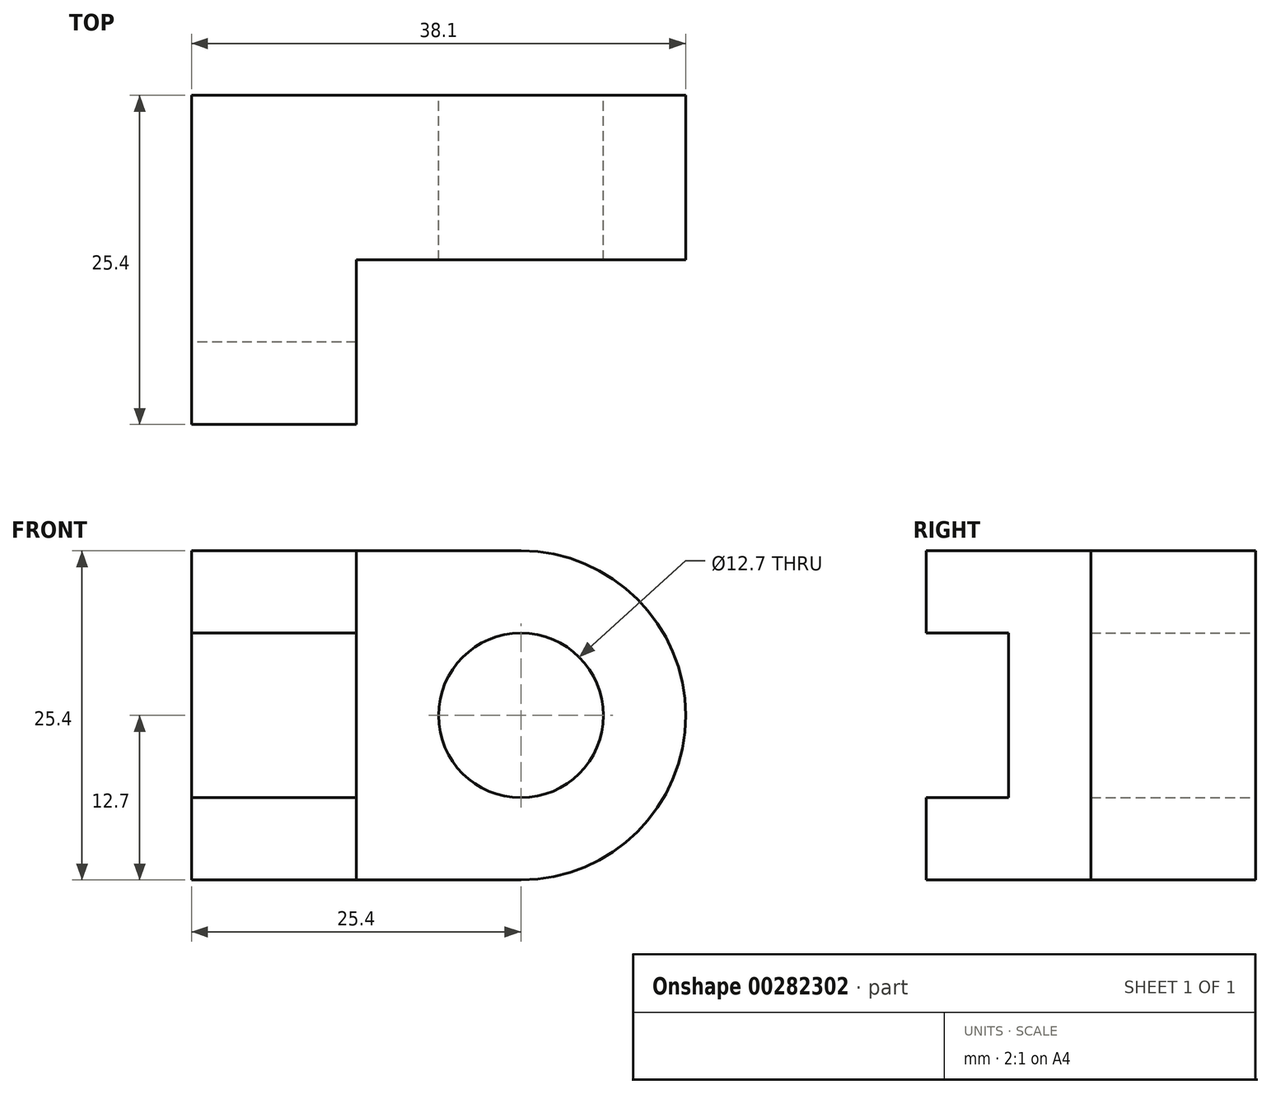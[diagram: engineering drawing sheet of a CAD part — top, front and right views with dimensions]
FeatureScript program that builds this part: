
annotation { "Feature Type Name" : "Feature", "Feature Type Description" : "" }
export const myFeature = defineFeature(function(context is Context, id is Id, definition is map)
    precondition{}
    {
        {
            var Q0;
            Q0=qCreatedBy(makeId("Front.planeOp"),FACE);
            var sketch = newSketch(context, id + "F0", { "sketchPlane" : qUnion([Q0])});
            skLineSegment(sketch, "E0", {"start": v(0, 0) * mm, "end": v(0, 25.4) * mm});
            skLineSegment(sketch, "E1", {"start": v(0, 25.4) * mm, "end": v(25.4, 25.4) * mm});
            skArc(sketch, "E2", {"start": v(25.4, 25.4) * mm, "mid": v(38.1, 12.7) * mm, "end": v(25.4, 0) * mm});
            skLineSegment(sketch, "E3", {"start": v(25.4, 0) * mm, "end": v(0, 0) * mm});
            skCircle(sketch, "E4", {"center": v(25.4, 12.7) * mm, "radius": 6.35 * mm});
            skSolve(sketch);
        }
        {
            var Q0;
            Q0=makeQuery(id+"F0.imprint","IMPRINT",FACE,{"disambiguationData":[TD([[makeQuery(id+"F0.imprint","IMPRINT",EDGE,{"derivedFrom":sQuery(id+"F0.wireOp",EDGE,"E0")}),-1.0]])]});
            extrude(context, id + "F1", {"entities" : qUnion([Q0]), "depth" : 12.7 * mm});
        }
        {
            var Q0;
            Q0=qCreatedBy(makeId("Front.planeOp"),FACE);
            var sketch = newSketch(context, id + "F2", { "sketchPlane" : qUnion([Q0])});
            skLineSegment(sketch, "E5.bottom", {"start": v(0, 0) * mm, "end": v(12.7, 0) * mm});
            skLineSegment(sketch, "E5.top", {"start": v(0, 25.4) * mm, "end": v(12.7, 25.4) * mm});
            skLineSegment(sketch, "E5.left", {"start": v(0, 0) * mm, "end": v(0, 25.4) * mm});
            skLineSegment(sketch, "E5.right", {"start": v(12.7, 0) * mm, "end": v(12.7, 25.4) * mm});
            skSolve(sketch);
        }
        {
            var Q0;
            Q0 = qSketchRegion(id + "F2", true);
            extrude(context, id + "F3", {"entities" : qUnion([Q0]), "operationType" : NewBodyOperationType.ADD, "depth" : 25.4 * mm});
        }
        {
            var Q0;
            Q0=qCreatedBy(makeId("Right.planeOp"),FACE);
            var sketch = newSketch(context, id + "F4", { "sketchPlane" : qUnion([Q0])});
            skLineSegment(sketch, "E6.bottom", {"start": v(-25.4, 19.05) * mm, "end": v(-19.05, 19.05) * mm});
            skLineSegment(sketch, "E6.top", {"start": v(-25.4, 6.35) * mm, "end": v(-19.05, 6.35) * mm});
            skLineSegment(sketch, "E6.left", {"start": v(-25.4, 19.05) * mm, "end": v(-25.4, 6.35) * mm});
            skLineSegment(sketch, "E6.right", {"start": v(-19.05, 19.05) * mm, "end": v(-19.05, 6.35) * mm});
            skSolve(sketch);
        }
        {
            var Q0;
            Q0 = qSketchRegion(id + "F4", true);
            extrude(context, id + "F5", {"entities" : qUnion([Q0]), "operationType" : NewBodyOperationType.REMOVE, "depth" : 50.3 * mm});
        }
    });
